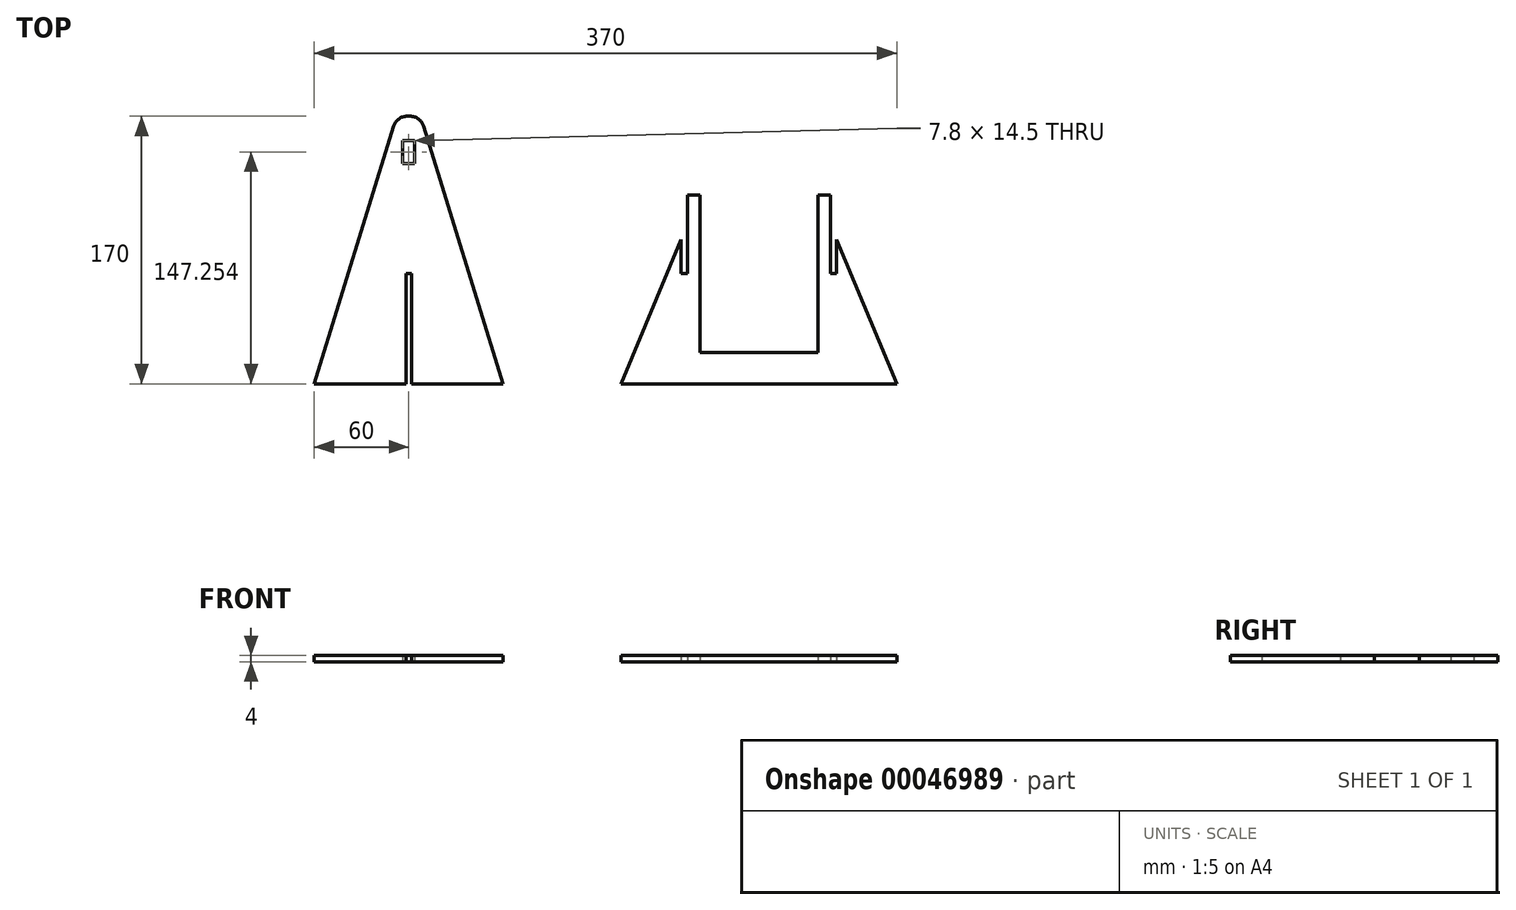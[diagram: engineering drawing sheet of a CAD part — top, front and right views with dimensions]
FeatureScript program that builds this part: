
annotation { "Feature Type Name" : "Feature", "Feature Type Description" : "" }
export const myFeature = defineFeature(function(context is Context, id is Id, definition is map)
    precondition{}
    {
        {
            var Q0;
            Q0=qCreatedBy(makeId("Top.planeOp"),FACE);
            var sketch = newSketch(context, id + "F0", { "sketchPlane" : qUnion([Q0])});
            skLineSegment(sketch, "E0.bottom", {"start": v(-63.9, 72.38) * mm, "end": v(-56.1, 72.38) * mm});
            skLineSegment(sketch, "E0.top", {"start": v(-63.9, 57.88) * mm, "end": v(-56.1, 57.88) * mm});
            skLineSegment(sketch, "E0.left", {"start": v(-63.9, 72.38) * mm, "end": v(-63.9, 57.88) * mm});
            skLineSegment(sketch, "E0.right", {"start": v(-56.1, 72.38) * mm, "end": v(-56.1, 57.88) * mm});
            skLineSegment(sketch, "E1.bottom", {"start": v(-60.86, 87.88) * mm, "end": v(-59.14, 87.88) * mm});
            skLineSegment(sketch, "E1.top", {"start": v(-61.77, -82.12) * mm, "end": v(-58.22, -82.12) * mm});
            skPoint(sketch, "E2", {"position": v(-60, 87.88) * mm});
            skPoint(sketch, "E3", {"position": v(-60, 72.38) * mm});
            skLineSegment(sketch, "E4", {"start": v(-60, 87.88) * mm, "end": v(-60, 72.38) * mm, "construction": true});
            skLineSegment(sketch, "E5", {"start": v(-50.54, 81.54) * mm, "end": v(0, -82.12) * mm});
            skLineSegment(sketch, "E6", {"start": v(-69.46, 81.54) * mm, "end": v(-120, -82.12) * mm});
            skLineSegment(sketch, "E7", {"start": v(-58.22, -82.12) * mm, "end": v(0, -82.12) * mm});
            skLineSegment(sketch, "E8", {"start": v(-61.77, -82.12) * mm, "end": v(-120, -82.12) * mm});
            skPoint(sketch, "E9.visualSharp", {"position": v(-52.5, 87.88) * mm});
            skArc(sketch, "E9.filletArc", {"start": v(-50.54, 81.54) * mm, "mid": v(-53.8, 86.13) * mm, "end": v(-59.14, 87.88) * mm});
            skPoint(sketch, "E10.visualSharp", {"position": v(-67.5, 87.88) * mm});
            skArc(sketch, "E10.filletArc", {"start": v(-60.86, 87.88) * mm, "mid": v(-66.2, 86.13) * mm, "end": v(-69.46, 81.54) * mm});
            skPoint(sketch, "E11", {"position": v(-60, -82.12) * mm});
            skLineSegment(sketch, "E12", {"start": v(-60, 57.88) * mm, "end": v(-60, -82.12) * mm, "construction": true});
            skLineSegment(sketch, "E13", {"start": v(-58.22, -82.12) * mm, "end": v(-58.22, -12.12) * mm});
            skLineSegment(sketch, "E14", {"start": v(-58.22, -12.12) * mm, "end": v(-61.77, -12.12) * mm});
            skLineSegment(sketch, "E15", {"start": v(-61.78, -12.12) * mm, "end": v(-61.78, -82.12) * mm});
            skLineSegment(sketch, "E16", {"start": v(200, -82.12) * mm, "end": v(250, -82.12) * mm});
            skLineSegment(sketch, "E17", {"start": v(200, -62.12) * mm, "end": v(200, 24.53) * mm});
            skLineSegment(sketch, "E18", {"start": v(211.85, 9.44) * mm, "end": v(250, -82.12) * mm});
            skPoint(sketch, "E19", {"position": v(208, 18.68) * mm});
            skPoint(sketch, "E20", {"position": v(211.85, 9.44) * mm});
            skLineSegment(sketch, "E21", {"start": v(211.85, 9.44) * mm, "end": v(211.85, 18.68) * mm, "construction": true});
            skLineSegment(sketch, "E22", {"start": v(208, 18.68) * mm, "end": v(208, -12.12) * mm});
            skLineSegment(sketch, "E23", {"start": v(208, -12.12) * mm, "end": v(211.85, -12.12) * mm});
            skLineSegment(sketch, "E24", {"start": v(211.85, -12.12) * mm, "end": v(211.85, 9.44) * mm});
            skLineSegment(sketch, "E25", {"start": v(208, 18.68) * mm, "end": v(208, 37.88) * mm});
            skLineSegment(sketch, "E26", {"start": v(208, 37.88) * mm, "end": v(200, 37.88) * mm});
            skLineSegment(sketch, "E27", {"start": v(162.5, -62.12) * mm, "end": v(162.5, 42.55) * mm, "construction": true});
            skLineSegment(sketch, "E28.MirrorCS", {"start": v(125, -62.12) * mm, "end": v(125, 24.53) * mm});
            skLineSegment(sketch, "E29.MirrorCS", {"start": v(125, -82.12) * mm, "end": v(75, -82.12) * mm});
            skLineSegment(sketch, "E30.MirrorCS", {"start": v(113.15, 9.44) * mm, "end": v(75, -82.12) * mm});
            skLineSegment(sketch, "E31.MirrorCS", {"start": v(117, 37.88) * mm, "end": v(125, 37.88) * mm});
            skLineSegment(sketch, "E32.MirrorCS", {"start": v(117, 18.68) * mm, "end": v(117, 37.88) * mm});
            skLineSegment(sketch, "E33.MirrorCS", {"start": v(117, 18.68) * mm, "end": v(117, -12.12) * mm});
            skLineSegment(sketch, "E34.MirrorCS", {"start": v(113.15, -12.12) * mm, "end": v(113.15, 9.44) * mm});
            skLineSegment(sketch, "E35.MirrorCS", {"start": v(117, -12.12) * mm, "end": v(113.15, -12.12) * mm});
            skPoint(sketch, "E36.orphan", {"position": v(117, 18.68) * mm});
            skLineSegment(sketch, "E37", {"start": v(125, -82.12) * mm, "end": v(200, -82.12) * mm});
            skLineSegment(sketch, "E38", {"start": v(125, -62.12) * mm, "end": v(200, -62.12) * mm});
            skPoint(sketch, "E39.orphan", {"position": v(125, 37.88) * mm});
            skPoint(sketch, "E40.orphan", {"position": v(125, -82.12) * mm});
            skLineSegment(sketch, "E41", {"start": v(200, 37.88) * mm, "end": v(200, 24.53) * mm});
            skLineSegment(sketch, "E42", {"start": v(125, 37.88) * mm, "end": v(125, 24.53) * mm});
            skSolve(sketch);
        }
        {
            var Q0;
            Q0=makeQuery(id+"F0.imprint","IMPRINT",FACE,{"disambiguationData":[TD([[makeQuery(id+"F0.imprint","IMPRINT",EDGE,{"derivedFrom":sQuery(id+"F0.wireOp",EDGE,"E0.bottom")}),1.0]])]});
            var Q1;
            {var subQ0=sQuery(id+"F0.wireOp",EDGE,"Ss4AIbZb-A55F-zNj1-JNTr-gfHRCLKZHlFp");Q1=makeQuery(id+"F0.imprint","IMPRINT",FACE,{"disambiguationData":[TD([[makeQuery(id+"F0.imprint","IMPRINT",EDGE,{"derivedFrom":subQ0}),-1.0]])]});}
            var Q2;
            {var subQ4=sQuery(id+"F0.wireOp",EDGE,"E16");Q2=makeQuery(id+"F0.imprint","IMPRINT",FACE,{"disambiguationData":[TD([[makeQuery(id+"F0.imprint","IMPRINT",EDGE,{"derivedFrom":subQ4}),1.0]])]});}
            var Q3;
            {var subQ3=sQuery(id+"F0.wireOp",EDGE,"E29.MirrorCS");Q3=makeQuery(id+"F0.imprint","IMPRINT",FACE,{"disambiguationData":[TD([[makeQuery(id+"F0.imprint","IMPRINT",EDGE,{"derivedFrom":subQ3}),-1.0]])]});}
            var Q4;
            {var subQ0=sQuery(id+"F0.wireOp",EDGE,"E37");Q4=makeQuery(id+"F0.imprint","IMPRINT",FACE,{"disambiguationData":[TD([[makeQuery(id+"F0.imprint","IMPRINT",EDGE,{"derivedFrom":subQ0}),1.0]])]});}
            extrude(context, id + "F1", {"entities" : qUnion([Q0, Q1, Q2, Q3, Q4]), "depth" : 4 * mm});
        }
    });
